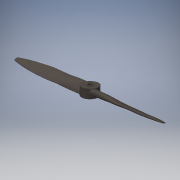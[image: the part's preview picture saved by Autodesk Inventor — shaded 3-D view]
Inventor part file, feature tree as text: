
AUTODESK INVENTOR PART (.ipt)
format: ipt  version: 2018 (Build 220112000, 112)  size: 1,660,416 bytes
history: native  units: mm
features: sketch x9, plane x7, other x3, revolve x1, loft x1, fillet x1, pattern_circular x1
ambient origin geometry x8: Origin, YZ Plane, XZ Plane, XY Plane, X Axis, Y Axis, Z Axis, Center Point
bodies: Solid1 (feature_tree)
feature tree (23):
  revolve  "Revolution1"  [1 undecoded]
  plane  "Work Plane1"
  plane  "Work Plane2"
  plane  "Work Plane3"
  plane  "Work Plane4"
  plane  "Work Plane5"
  plane  "Work Plane6"
  sketch  "Sketch2"  dims[d2=3.0mm d3=1.5mm d4=22.0mm]
  sketch  "Sketch3"  dims[d5=2.0mm]
  sketch  "Sketch4"  dims[d6=1.5mm]
  sketch  "Sketch5"  dims[d7=1.5mm]
  sketch  "Sketch6"  dims[d8=90.0deg]
  sketch  "Sketch7"  dims[d9=56.14mm d10=96.77mm d11=126.14mm d12=157.8mm d13=189.33mm d14=220.0mm d20=40.0mm]
  plane  "Work Plane7"
  sketch  "Sketch8"  dims[d24=33.278655mm]
  loft  "Loft1"
  fillet  "Fillet1"  Radius=22.0mm
  other  "Work Axis1"
  pattern_circular  "Circular Pattern1"  Count=4  [1 undecoded]
  sketch  "Sketch1"  dims[d0=5.0mm d1=20.0mm]
  other  "Image1"
  sketch  "Sketch10"  dims[d76=8.695358mm d84=13.02mm d85=15.153mm d86=15.153mm d87=13.012mm d88=9.821mm d95=13.02mm d96=15.153mm d97=15.153mm d98=13.012mm d99=9.821mm d100=221.460376mm d102=176.089529mm d131=13.02mm d132=10.0mm d135=15.153mm d136=10.0mm d142=10.0mm d143=15.153mm d150=13.012mm d151=10.0mm d152=9.821mm d153=10.0mm d154=12.0mm d155=0.0mm d156=90.0deg d157=0.0mm d158=90.0deg d159=0.0mm d160=90.0deg d161=0.0mm d162=90.0deg d163=0.0mm d164=90.0deg d165=0.0mm d166=90.0deg d167=0.0mm d168=90.0deg d169=2.0mm d170=2.0mm d171=2.0mm d172=7.436mm d173=2.0mm d174=7.969mm d175=2.0mm d176=5.859mm d177=2.0mm d178=0.313mm d179=2.0mm d180=8.125mm d181=2.0mm d182=9.277mm d183=2.0mm d184=1.18mm d185=20.0mm d186=360.0deg]
  other  "Work Axis2"
note: 2 required parameter values undecoded (feature->parameter linkage not recoverable at this tier; creation-order binding heuristic only, values carry confidence <= 0.55)